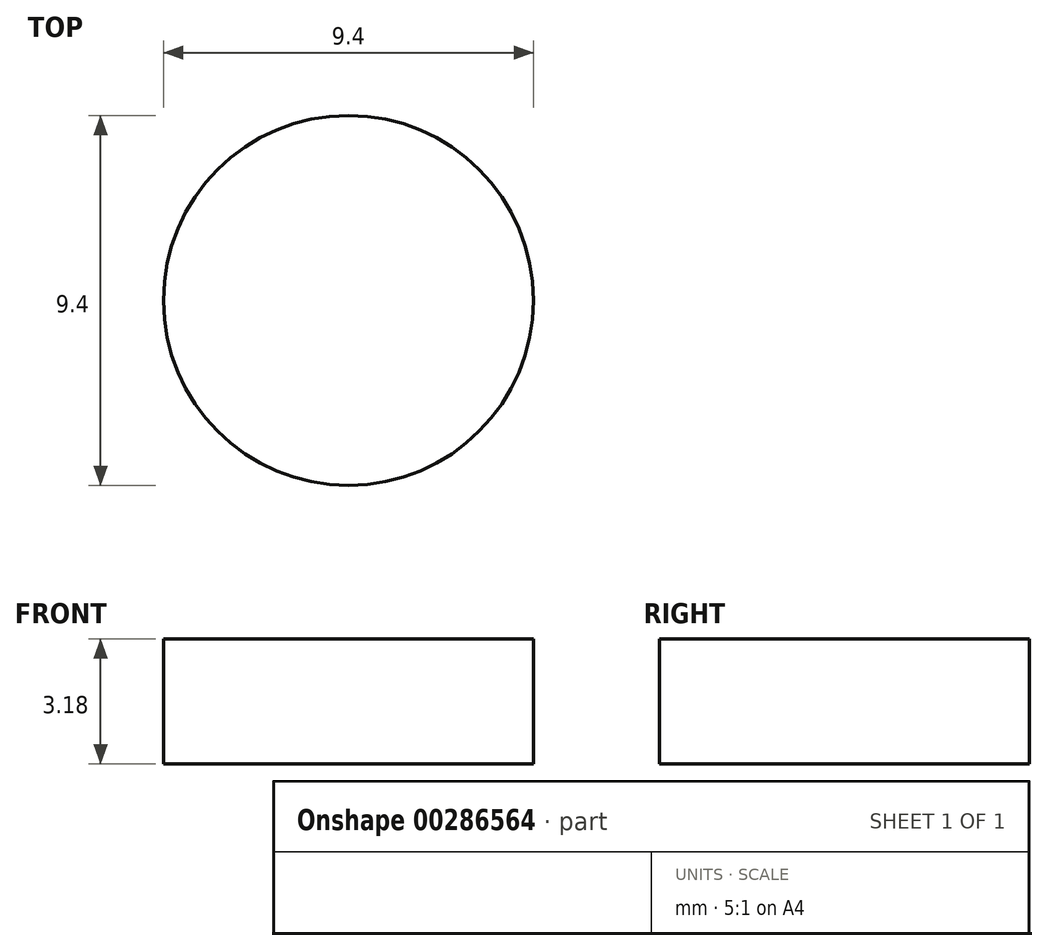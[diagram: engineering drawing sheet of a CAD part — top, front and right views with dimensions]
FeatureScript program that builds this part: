
annotation { "Feature Type Name" : "Feature", "Feature Type Description" : "" }
export const myFeature = defineFeature(function(context is Context, id is Id, definition is map)
    precondition{}
    {
        {
            var Q0;
            Q0=qCreatedBy(makeId("Top.planeOp"),FACE);
            var sketch = newSketch(context, id + "F0", { "sketchPlane" : qUnion([Q0])});
            skCircle(sketch, "E0", {"center": v(0, 0) * mm, "radius": 12.7 * mm});
            skCircle(sketch, "E1", {"center": v(-6.4, 4.8) * mm, "radius": 4.7 * mm});
            skSolve(sketch);
        }
        {
            var Q0;
            Q0=makeQuery(id+"F0.imprint","IMPRINT",FACE,{"disambiguationData":[TD([[makeQuery(id+"F0.imprint","IMPRINT",EDGE,{"derivedFrom":sQuery(id+"F0.wireOp",EDGE,"E1")}),1.0]])]});
            extrude(context, id + "F1", {"entities" : qUnion([Q0]), "depth" : 3.17 * mm});
        }
    });
